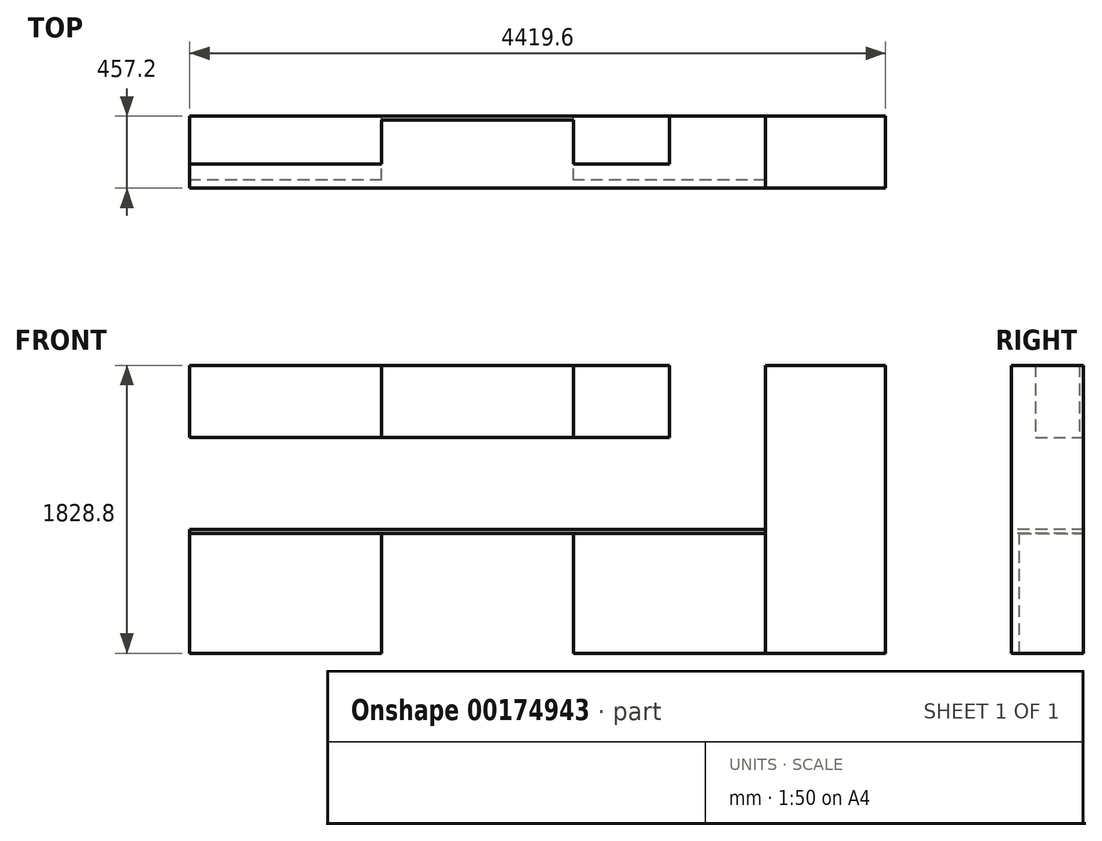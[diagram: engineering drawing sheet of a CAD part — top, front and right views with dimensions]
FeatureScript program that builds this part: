
annotation { "Feature Type Name" : "Feature", "Feature Type Description" : "" }
export const myFeature = defineFeature(function(context is Context, id is Id, definition is map)
    precondition{}
    {
        {
            var Q0;
            Q0=qCreatedBy(makeId("Front.planeOp"),FACE);
            var sketch = newSketch(context, id + "F0", { "sketchPlane" : qUnion([Q0])});
            skLineSegment(sketch, "E0.bottom", {"start": v(914.4, -381) * mm, "end": v(-914.4, -381) * mm});
            skLineSegment(sketch, "E0.top", {"start": v(914.4, 381) * mm, "end": v(-914.4, 381) * mm});
            skLineSegment(sketch, "E0.left", {"start": v(914.4, -381) * mm, "end": v(914.4, 381) * mm});
            skLineSegment(sketch, "E0.right", {"start": v(-914.4, -381) * mm, "end": v(-914.4, 381) * mm});
            skPoint(sketch, "E0.middle", {"position": v(0, 0) * mm});
            skLineSegment(sketch, "E1", {"start": v(-914.4, -584.2) * mm, "end": v(914.4, -584.2) * mm});
            skLineSegment(sketch, "E2", {"start": v(304.8, 381) * mm, "end": v(304.8, -381) * mm});
            skLineSegment(sketch, "E3", {"start": v(-304.8, 381) * mm, "end": v(-304.8, -381) * mm});
            skLineSegment(sketch, "E4.bottom", {"start": v(914.4, -381) * mm, "end": v(1524, -381) * mm});
            skLineSegment(sketch, "E4.top", {"start": v(914.4, 381) * mm, "end": v(1524, 381) * mm});
            skLineSegment(sketch, "E4.right", {"start": v(1524, -381) * mm, "end": v(1524, 381) * mm});
            skLineSegment(sketch, "E5.bottom", {"start": v(1524, -381) * mm, "end": v(2286, -381) * mm});
            skLineSegment(sketch, "E5.top", {"start": v(1524, 1447.8) * mm, "end": v(2286, 1447.8) * mm});
            skLineSegment(sketch, "E5.left", {"start": v(1524, -381) * mm, "end": v(1524, 1447.8) * mm});
            skLineSegment(sketch, "E5.right", {"start": v(2286, -381) * mm, "end": v(2286, 1447.8) * mm});
            skLineSegment(sketch, "E6.bottom", {"start": v(-914.4, -381) * mm, "end": v(-1524, -381) * mm});
            skLineSegment(sketch, "E6.right", {"start": v(-1524, -381) * mm, "end": v(-1524, 381) * mm});
            skLineSegment(sketch, "E7.bottom", {"start": v(-1524, -381) * mm, "end": v(-2133.6, -381) * mm});
            skLineSegment(sketch, "E7.top", {"start": v(-1524, 381) * mm, "end": v(-2133.6, 381) * mm});
            skLineSegment(sketch, "E7.right", {"start": v(-2133.6, -381) * mm, "end": v(-2133.6, 381) * mm});
            skLineSegment(sketch, "E8.bottom", {"start": v(-914.4, 1447.8) * mm, "end": v(-304.8, 1447.8) * mm});
            skLineSegment(sketch, "E8.top", {"start": v(-914.4, 990.6) * mm, "end": v(-304.8, 990.6) * mm});
            skLineSegment(sketch, "E8.right", {"start": v(1524, 1447.8) * mm, "end": v(1524, 990.6) * mm});
            skLineSegment(sketch, "E9", {"start": v(-914.4, 1447.8) * mm, "end": v(-914.4, 990.6) * mm});
            skLineSegment(sketch, "E10", {"start": v(-1524, 381) * mm, "end": v(-914.4, 381) * mm});
            skLineSegment(sketch, "E11.bottom", {"start": v(-914.4, 990.6) * mm, "end": v(-1524, 990.6) * mm});
            skLineSegment(sketch, "E11.top", {"start": v(-914.4, 1447.8) * mm, "end": v(-1524, 1447.8) * mm});
            skLineSegment(sketch, "E11.left", {"start": v(-914.4, 990.6) * mm, "end": v(-914.4, 1447.8) * mm});
            skLineSegment(sketch, "E11.right", {"start": v(-1524, 990.6) * mm, "end": v(-1524, 1447.8) * mm});
            skLineSegment(sketch, "E12.bottom", {"start": v(-1524, 1447.8) * mm, "end": v(-2133.6, 1447.8) * mm});
            skLineSegment(sketch, "E12.top", {"start": v(-1524, 990.6) * mm, "end": v(-2133.6, 990.6) * mm});
            skLineSegment(sketch, "E12.left", {"start": v(-1524, 1447.8) * mm, "end": v(-1524, 990.6) * mm});
            skLineSegment(sketch, "E12.right", {"start": v(-2133.6, 1447.8) * mm, "end": v(-2133.6, 990.6) * mm});
            skLineSegment(sketch, "E13", {"start": v(-304.8, 1447.8) * mm, "end": v(-304.8, 990.6) * mm});
            skLineSegment(sketch, "E14", {"start": v(304.8, 1447.8) * mm, "end": v(304.8, 990.6) * mm});
            skLineSegment(sketch, "E15.trimOffspring", {"start": v(304.8, 1447.8) * mm, "end": v(1524, 1447.8) * mm});
            skLineSegment(sketch, "E16.trimOffspring", {"start": v(304.8, 990.6) * mm, "end": v(1524, 990.6) * mm});
            skLineSegment(sketch, "E17", {"start": v(-304.8, 1447.8) * mm, "end": v(304.8, 1447.8) * mm});
            skLineSegment(sketch, "E18", {"start": v(-304.8, 990.6) * mm, "end": v(304.8, 990.6) * mm});
            skLineSegment(sketch, "E19", {"start": v(914.4, 1447.8) * mm, "end": v(914.4, 990.6) * mm});
            skSolve(sketch);
        }
        {
            var Q0;
            {var subQ2=sQuery(id+"F0.wireOp",EDGE,"E2");Q0=makeQuery(id+"F0.imprint","IMPRINT",FACE,{"disambiguationData":[TD([[makeQuery(id+"F0.imprint","IMPRINT",EDGE,{"derivedFrom":subQ2}),1.0]])]});}
            var Q1;
            Q1=makeQuery(id+"F0.imprint","IMPRINT",FACE,{"disambiguationData":[TD([[makeQuery(id+"F0.imprint","IMPRINT",EDGE,{"derivedFrom":sQuery(id+"F0.wireOp",EDGE,"E7.bottom")}),-1.0]])]});
            var Q2;
            Q2=makeQuery(id+"F0.imprint","IMPRINT",FACE,{"disambiguationData":[TD([[makeQuery(id+"F0.imprint","IMPRINT",EDGE,{"derivedFrom":sQuery(id+"F0.wireOp",EDGE,"E6.bottom")}),-1.0]])]});
            var Q3;
            {var subQ0=sQuery(id+"F0.wireOp",EDGE,"E4.bottom");Q3=makeQuery(id+"F0.imprint","IMPRINT",FACE,{"disambiguationData":[TD([[makeQuery(id+"F0.imprint","IMPRINT",EDGE,{"derivedFrom":subQ0}),1.0]])]});}
            extrude(context, id + "F1", {"entities" : qUnion([Q0, Q1, Q2, Q3]), "depth" : 406.4 * mm, "offsetDistance" : 25.4 * mm});
        }
        {
            var Q0;
            {var subQ3=sQuery(id+"F0.wireOp",EDGE,"E5.bottom");Q0=makeQuery(id+"F0.imprint","IMPRINT",FACE,{"disambiguationData":[TD([[makeQuery(id+"F0.imprint","IMPRINT",EDGE,{"derivedFrom":subQ3}),1.0]])]});}
            extrude(context, id + "F2", {"entities" : qUnion([Q0]), "operationType" : NewBodyOperationType.ADD, "depth" : 457.2 * mm, "offsetDistance" : 25.4 * mm});
        }
        {
            var Q0;
            Q0=makeQuery(id+"F0.imprint","IMPRINT",FACE,{"disambiguationData":[TD([[makeQuery(id+"F0.imprint","IMPRINT",EDGE,{"derivedFrom":sQuery(id+"F0.wireOp",EDGE,"E11.bottom")}),-1.0]])]});
            var Q1;
            Q1=makeQuery(id+"F0.imprint","IMPRINT",FACE,{"disambiguationData":[TD([[makeQuery(id+"F0.imprint","IMPRINT",EDGE,{"derivedFrom":sQuery(id+"F0.wireOp",EDGE,"E12.bottom")}),1.0]])]});
            var Q2;
            {var subQ0=sQuery(id+"F0.wireOp",EDGE,"E14");Q2=makeQuery(id+"F0.imprint","IMPRINT",FACE,{"disambiguationData":[TD([[makeQuery(id+"F0.imprint","IMPRINT",EDGE,{"derivedFrom":subQ0}),1.0]])]});}
            var Q3;
            {var subQ0=sQuery(id+"F0.wireOp",EDGE,"E8.right");Q3=makeQuery(id+"F0.imprint","IMPRINT",FACE,{"disambiguationData":[TD([[makeQuery(id+"F0.imprint","IMPRINT",EDGE,{"derivedFrom":subQ0}),-1.0]])]});}
            extrude(context, id + "F3", {"entities" : qUnion([Q0, Q1, Q2, Q3]), "operationType" : NewBodyOperationType.ADD, "depth" : 304.8 * mm, "offsetDistance" : 25.4 * mm});
        }
        {
            var Q0;
            Q0=makeQuery(id+"F1.opExtrude","SWEPT_FACE",FACE,{"disambiguationData":[OSD([sQuery(id+"F0.wireOp",EDGE,"E7.top"),sQuery(id+"F0.wireOp",EDGE,"E10")])]});
            var sketch = newSketch(context, id + "F4", { "sketchPlane" : qUnion([Q0])});
            skLineSegment(sketch, "E20.bottom", {"start": v(1523.58, 0) * mm, "end": v(-2133.6, 0) * mm});
            skLineSegment(sketch, "E20.top", {"start": v(1523.58, -457.2) * mm, "end": v(-2133.6, -457.2) * mm});
            skLineSegment(sketch, "E20.left", {"start": v(1523.58, 0) * mm, "end": v(1523.58, -457.2) * mm});
            skLineSegment(sketch, "E20.right", {"start": v(-2133.6, 0) * mm, "end": v(-2133.6, -457.2) * mm});
            skSolve(sketch);
        }
        {
            var Q0;
            {var subQ1=sQuery(id+"F0.wireOp",EDGE,"E10");var subQ5=makeQuery(id+"F1.opExtrude","CAP_EDGE",EDGE,{"disambiguationData":[OSD([sQuery(id+"F0.wireOp",EDGE,"E7.top"),subQ1])],"isStart":false});Q0=makeQuery(id+"F4.imprint","IMPRINT",FACE,{"disambiguationData":[TD([[makeQuery(id+"F4.imprint","IMPRINT",EDGE,{"derivedFrom":subQ5}),-1.0]])]});}
            var Q1;
            {var subQ1=sQuery(id+"F4.wireOp",EDGE,"E20.top");Q1=makeQuery(id+"F4.imprint","IMPRINT",FACE,{"disambiguationData":[TD([[makeQuery(id+"F4.imprint","IMPRINT",EDGE,{"derivedFrom":subQ1}),-1.0]])]});}
            extrude(context, id + "F5", {"entities" : qUnion([Q0, Q1]), "depth" : 25.4 * mm, "offsetDistance" : 25.4 * mm});
        }
        {
            var Q0;
            Q0=makeQuery(id+"F0.imprint","IMPRINT",FACE,{"disambiguationData":[TD([[makeQuery(id+"F0.imprint","IMPRINT",EDGE,{"derivedFrom":sQuery(id+"F0.wireOp",EDGE,"E13")}),1.0]])]});
            var Q1;
            Q1=makeQuery(id+"F0.imprint","IMPRINT",FACE,{"disambiguationData":[TD([[makeQuery(id+"F0.imprint","IMPRINT",EDGE,{"derivedFrom":sQuery(id+"F0.wireOp",EDGE,"E8.bottom")}),-1.0]])]});
            extrude(context, id + "F6", {"entities" : qUnion([Q0, Q1]), "operationType" : NewBodyOperationType.ADD, "depth" : 25.4 * mm, "offsetDistance" : 25.4 * mm});
        }
    });
